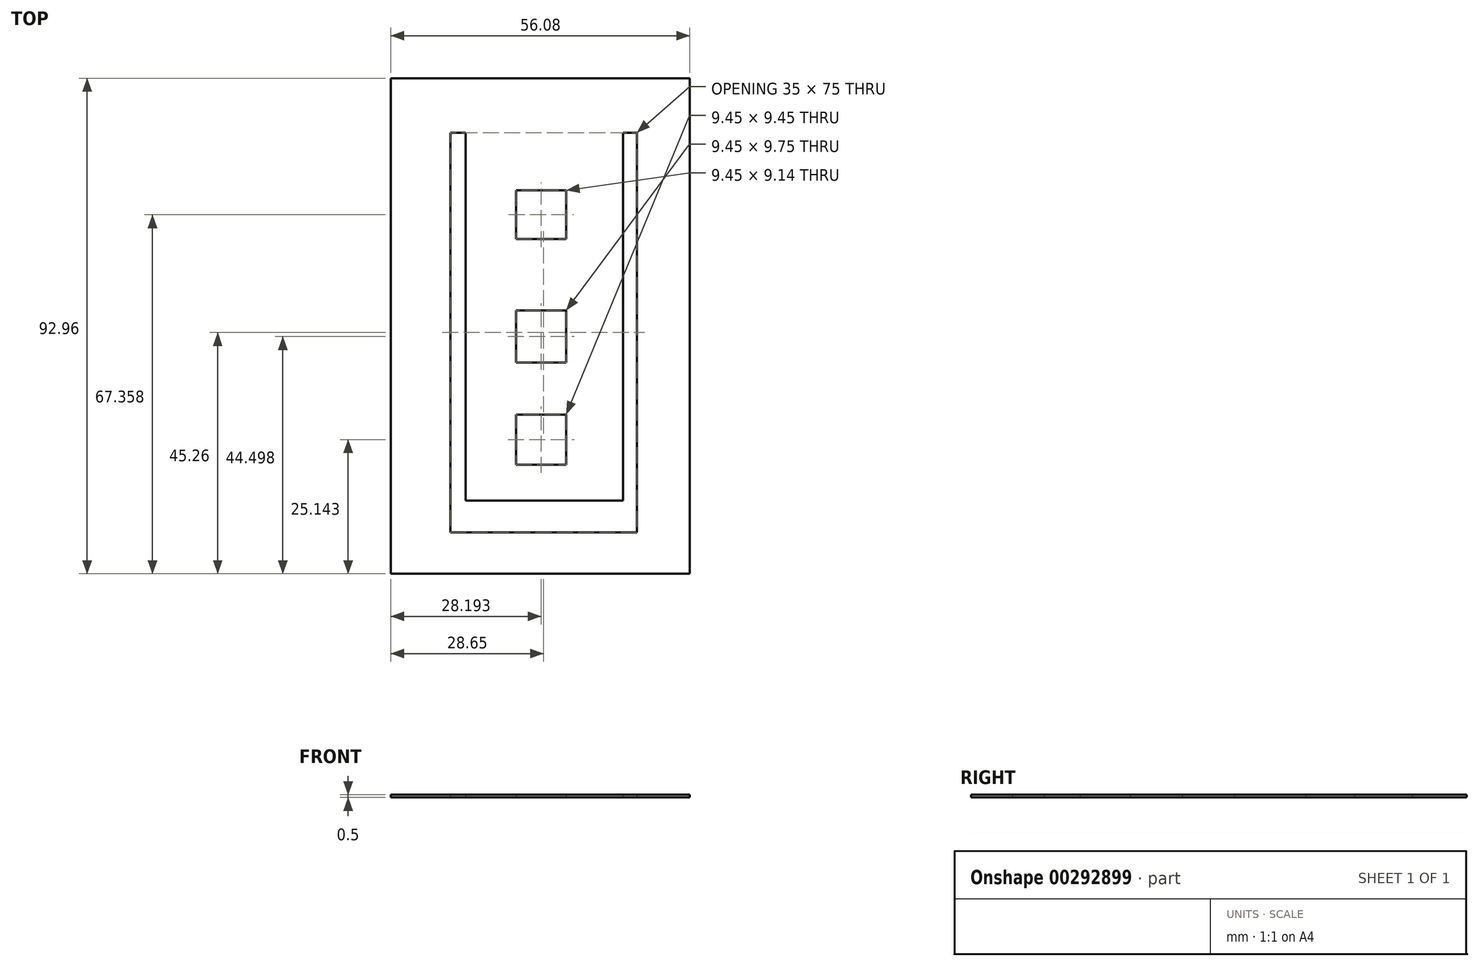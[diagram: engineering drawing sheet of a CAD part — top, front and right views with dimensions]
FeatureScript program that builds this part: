
annotation { "Feature Type Name" : "Feature", "Feature Type Description" : "" }
export const myFeature = defineFeature(function(context is Context, id is Id, definition is map)
    precondition{}
    {
        {
            var Q0;
            Q0=qCreatedBy(makeId("Top.planeOp"),FACE);
            var sketch = newSketch(context, id + "F0", { "sketchPlane" : qUnion([Q0])});
            skLineSegment(sketch, "E0.bottom", {"start": v(-17.5, 37.5) * mm, "end": v(-14.63, 37.5) * mm});
            skLineSegment(sketch, "E0.top", {"start": v(-17.5, -37.5) * mm, "end": v(17.5, -37.5) * mm});
            skLineSegment(sketch, "E0.left", {"start": v(-17.5, 37.5) * mm, "end": v(-17.5, -37.5) * mm});
            skLineSegment(sketch, "E0.right", {"start": v(17.5, 37.5) * mm, "end": v(17.5, -37.5) * mm});
            skPoint(sketch, "E0.middle", {"position": v(0, 0) * mm});
            skLineSegment(sketch, "E1.top", {"start": v(-14.63, -31.55) * mm, "end": v(14.94, -31.55) * mm});
            skLineSegment(sketch, "E1.left", {"start": v(-14.63, 37.5) * mm, "end": v(-14.63, -31.55) * mm});
            skLineSegment(sketch, "E1.right", {"start": v(14.94, 37.5) * mm, "end": v(14.94, -31.55) * mm});
            skLineSegment(sketch, "E2.bottom", {"start": v(-28.65, 47.7) * mm, "end": v(27.43, 47.7) * mm});
            skLineSegment(sketch, "E2.top", {"start": v(-28.65, -45.26) * mm, "end": v(27.43, -45.26) * mm});
            skLineSegment(sketch, "E2.left", {"start": v(-28.65, 47.7) * mm, "end": v(-28.65, -45.26) * mm});
            skLineSegment(sketch, "E2.right", {"start": v(27.43, 47.7) * mm, "end": v(27.43, -45.26) * mm});
            skLineSegment(sketch, "E3.bottom", {"start": v(-5.18, 26.67) * mm, "end": v(4.27, 26.67) * mm});
            skLineSegment(sketch, "E3.top", {"start": v(-5.18, 17.53) * mm, "end": v(4.27, 17.53) * mm});
            skLineSegment(sketch, "E3.left", {"start": v(-5.18, 26.67) * mm, "end": v(-5.18, 17.53) * mm});
            skLineSegment(sketch, "E3.right", {"start": v(4.27, 26.67) * mm, "end": v(4.27, 17.53) * mm});
            skLineSegment(sketch, "E4.bottom", {"start": v(-5.18, 4.11) * mm, "end": v(4.27, 4.11) * mm});
            skLineSegment(sketch, "E4.top", {"start": v(-5.18, -5.64) * mm, "end": v(4.27, -5.64) * mm});
            skLineSegment(sketch, "E4.left", {"start": v(-5.18, 4.11) * mm, "end": v(-5.18, -5.64) * mm});
            skLineSegment(sketch, "E4.right", {"start": v(4.27, 4.11) * mm, "end": v(4.27, -5.64) * mm});
            skLineSegment(sketch, "E5.bottom", {"start": v(-5.18, -15.4) * mm, "end": v(4.27, -15.4) * mm});
            skLineSegment(sketch, "E5.top", {"start": v(-5.18, -24.84) * mm, "end": v(4.27, -24.84) * mm});
            skLineSegment(sketch, "E5.left", {"start": v(-5.18, -15.4) * mm, "end": v(-5.18, -24.84) * mm});
            skLineSegment(sketch, "E5.right", {"start": v(4.27, -15.4) * mm, "end": v(4.27, -24.84) * mm});
            skLineSegment(sketch, "E6.trimOffspring", {"start": v(14.94, 37.5) * mm, "end": v(17.5, 37.5) * mm});
            skSolve(sketch);
        }
        {
            var Q0;
            Q0=makeQuery(id+"F0.imprint","IMPRINT",FACE,{"disambiguationData":[TD([[makeQuery(id+"F0.imprint","IMPRINT",EDGE,{"derivedFrom":sQuery(id+"F0.wireOp",EDGE,"E0.bottom")}),1.0]])]});
            extrude(context, id + "F1", {"entities" : qUnion([Q0]), "depth" : 0.5 * mm});
        }
    });
